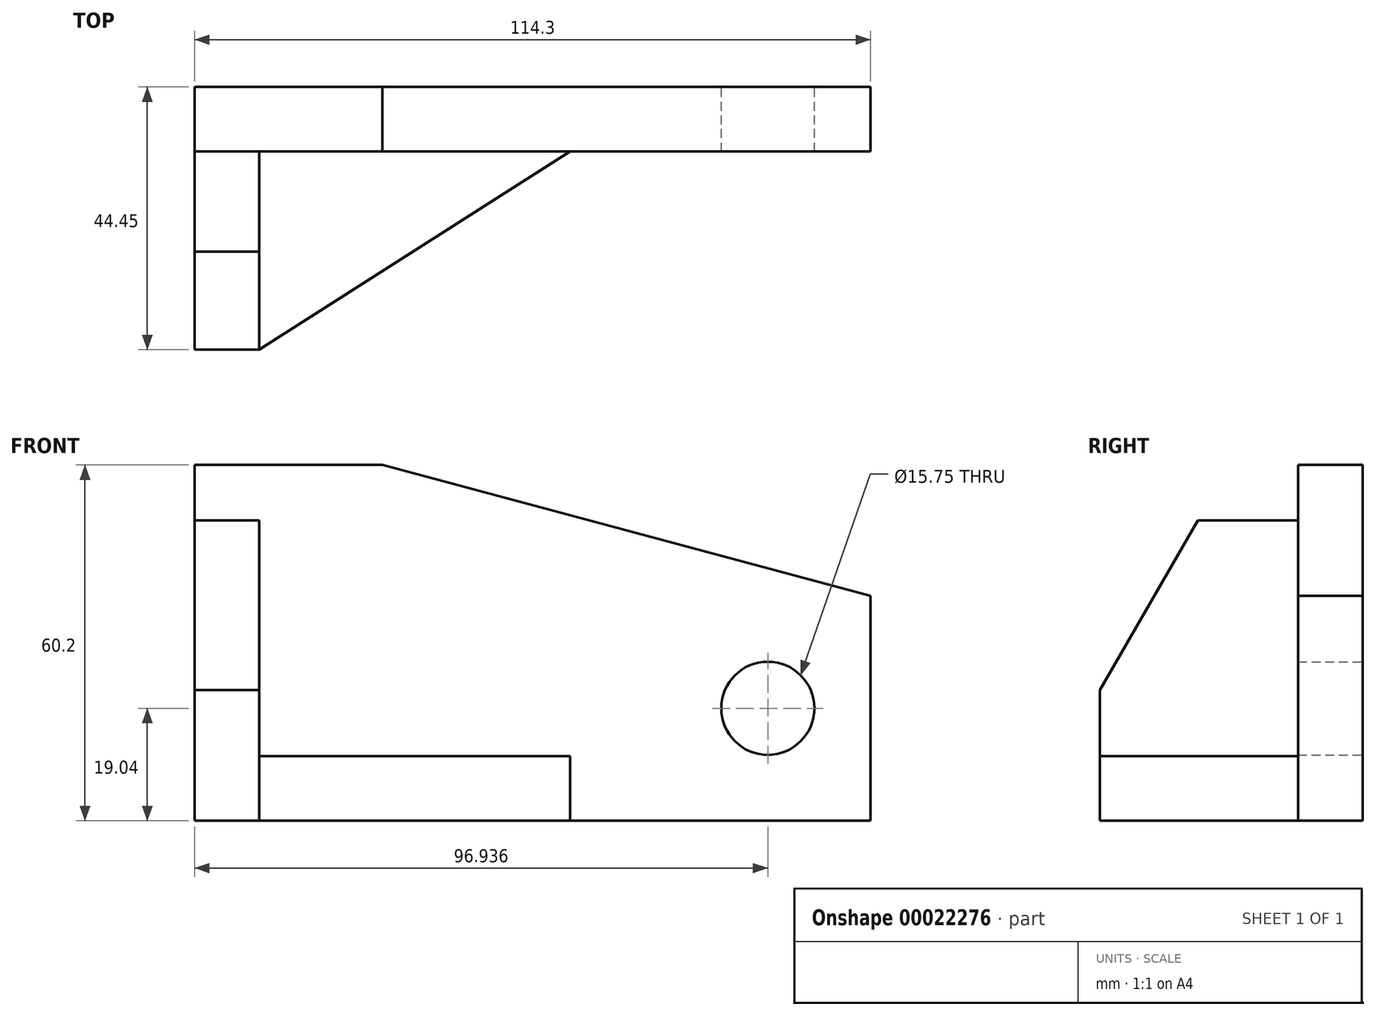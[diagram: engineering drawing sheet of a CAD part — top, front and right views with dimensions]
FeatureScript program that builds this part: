
annotation { "Feature Type Name" : "Feature", "Feature Type Description" : "" }
export const myFeature = defineFeature(function(context is Context, id is Id, definition is map)
    precondition{}
    {
        {
            var Q0;
            Q0=qCreatedBy(makeId("Front.planeOp"),FACE);
            var sketch = newSketch(context, id + "F0", { "sketchPlane" : qUnion([Q0])});
            skLineSegment(sketch, "E0.rect.bottom", {"start": v(-57.15, 30.1) * mm, "end": v(57.15, 30.1) * mm});
            skLineSegment(sketch, "E0.rect.top", {"start": v(-57.15, -30.1) * mm, "end": v(57.15, -30.1) * mm});
            skLineSegment(sketch, "E0.rect.left", {"start": v(-57.15, 30.1) * mm, "end": v(-57.15, -30.1) * mm});
            skLineSegment(sketch, "E0.rect.right", {"start": v(57.15, 30.1) * mm, "end": v(57.15, -30.1) * mm});
            skPoint(sketch, "E0.rect.middle", {"position": v(0, 0) * mm});
            skLineSegment(sketch, "E1", {"start": v(-25.4, 30.1) * mm, "end": v(57.15, 7.98) * mm});
            skCircle(sketch, "E2", {"center": v(39.79, -11.06) * mm, "radius": 7.87 * mm});
            skSolve(sketch);
        }
        {
            var Q0;
            {var subQ2=sQuery(id+"F0.wireOp",EDGE,"E0.rect.top");Q0=makeQuery(id+"F0.imprint","IMPRINT",FACE,{"disambiguationData":[TD([[makeQuery(id+"F0.imprint","IMPRINT",EDGE,{"derivedFrom":subQ2}),1.0]])]});}
            extrude(context, id + "F1", {"entities" : qUnion([Q0]), "depth" : 10.92 * mm});
        }
        {
            var Q0;
            Q0=makeQuery(id+"F1.opExtrude","CAP_FACE",FACE,{"disambiguationData":[OSD([sQuery(id+"F0.wireOp",EDGE,"E0.rect.bottom"),sQuery(id+"F0.wireOp",EDGE,"E0.rect.top"),sQuery(id+"F0.wireOp",EDGE,"E0.rect.left"),sQuery(id+"F0.wireOp",EDGE,"E0.rect.right"),sQuery(id+"F0.wireOp",EDGE,"E1"),sQuery(id+"F0.wireOp",EDGE,"E2")])],"isStart":false});
            var sketch = newSketch(context, id + "F2", { "sketchPlane" : qUnion([Q0])});
            skLineSegment(sketch, "E3.bottom", {"start": v(-57.15, 20.7) * mm, "end": v(-46.23, 20.7) * mm});
            skLineSegment(sketch, "E3.top", {"start": v(-57.15, -30.1) * mm, "end": v(-46.23, -30.1) * mm});
            skLineSegment(sketch, "E3.left", {"start": v(-57.15, 20.7) * mm, "end": v(-57.15, -30.1) * mm});
            skLineSegment(sketch, "E3.right", {"start": v(-46.23, 20.7) * mm, "end": v(-46.23, -30.1) * mm});
            skSolve(sketch);
        }
        {
            var Q0;
            Q0=makeQuery(id+"F2.imprint","IMPRINT",FACE,{"disambiguationData":[TD([[makeQuery(id+"F2.imprint","IMPRINT",EDGE,{"derivedFrom":sQuery(id+"F2.wireOp",EDGE,"E3.bottom")}),-1.0]])]});
            extrude(context, id + "F3", {"entities" : qUnion([Q0]), "operationType" : NewBodyOperationType.ADD, "depth" : 33.53 * mm});
        }
        {
            var Q0;
            Q0=makeQuery(id+"F3.opExtrude","SWEPT_FACE",FACE,{"disambiguationData":[OSD([sQuery(id+"F2.wireOp",EDGE,"E3.right")])]});
            var sketch = newSketch(context, id + "F4", { "sketchPlane" : qUnion([Q0])});
            skLineSegment(sketch, "E4", {"start": v(-27.88, 20.7) * mm, "end": v(-44.45, -8) * mm});
            skSolve(sketch);
        }
        {
            var Q0;
            {var subQ2=sQuery(id+"F4.wireOp",EDGE,"E4");Q0=makeQuery(id+"F4.imprint","IMPRINT",FACE,{"disambiguationData":[TD([[makeQuery(id+"F4.imprint","IMPRINT",EDGE,{"derivedFrom":subQ2}),-1.0]])]});}
            extrude(context, id + "F5", {"entities" : qUnion([Q0]), "operationType" : NewBodyOperationType.REMOVE, "oppositeDirection" : true, "depth" : 10.92 * mm});
        }
        {
            var Q0;
            Q0=makeQuery(id+"F1.opExtrude","CAP_FACE",FACE,{"disambiguationData":[OSD([sQuery(id+"F0.wireOp",EDGE,"E0.rect.bottom"),sQuery(id+"F0.wireOp",EDGE,"E0.rect.top"),sQuery(id+"F0.wireOp",EDGE,"E0.rect.left"),sQuery(id+"F0.wireOp",EDGE,"E0.rect.right"),sQuery(id+"F0.wireOp",EDGE,"E1"),sQuery(id+"F0.wireOp",EDGE,"E2")])],"isStart":false});
            var sketch = newSketch(context, id + "F6", { "sketchPlane" : qUnion([Q0])});
            skLineSegment(sketch, "E5.bottom", {"start": v(-46.23, -19.18) * mm, "end": v(6.35, -19.18) * mm});
            skLineSegment(sketch, "E5.top", {"start": v(-46.23, -30.1) * mm, "end": v(6.35, -30.1) * mm});
            skLineSegment(sketch, "E5.left", {"start": v(-46.23, -19.18) * mm, "end": v(-46.23, -30.1) * mm});
            skLineSegment(sketch, "E5.right", {"start": v(6.35, -19.18) * mm, "end": v(6.35, -30.1) * mm});
            skSolve(sketch);
        }
        {
            var Q0;
            Q0=makeQuery(id+"F6.imprint","IMPRINT",FACE,{"disambiguationData":[TD([[makeQuery(id+"F6.imprint","IMPRINT",EDGE,{"derivedFrom":sQuery(id+"F6.wireOp",EDGE,"E5.bottom")}),-1.0]])]});
            extrude(context, id + "F7", {"entities" : qUnion([Q0]), "depth" : 33.53 * mm});
        }
        {
            var Q0;
            Q0=makeQuery(id+"F7.opExtrude","SWEPT_FACE",FACE,{"disambiguationData":[OSD([sQuery(id+"F6.wireOp",EDGE,"E5.bottom")])]});
            var sketch = newSketch(context, id + "F8", { "sketchPlane" : qUnion([Q0])});
            skLineSegment(sketch, "E6", {"start": v(-46.23, -44.45) * mm, "end": v(6.35, -10.92) * mm});
            skSolve(sketch);
        }
        {
            var Q0;
            Q0 = qSketchRegion(id + "F8", true);
            var Q1;
            Q1=makeQuery(id+"F8.imprint","IMPRINT",FACE,{"disambiguationData":[TD([[makeQuery(id+"F8.imprint","IMPRINT",EDGE,{"derivedFrom":sQuery(id+"F8.wireOp",EDGE,"E6")}),-1.0]])]});
            extrude(context, id + "F9", {"entities" : qUnion([Q0, Q1]), "operationType" : NewBodyOperationType.REMOVE, "oppositeDirection" : true, "depth" : 10.92 * mm});
        }
    });
